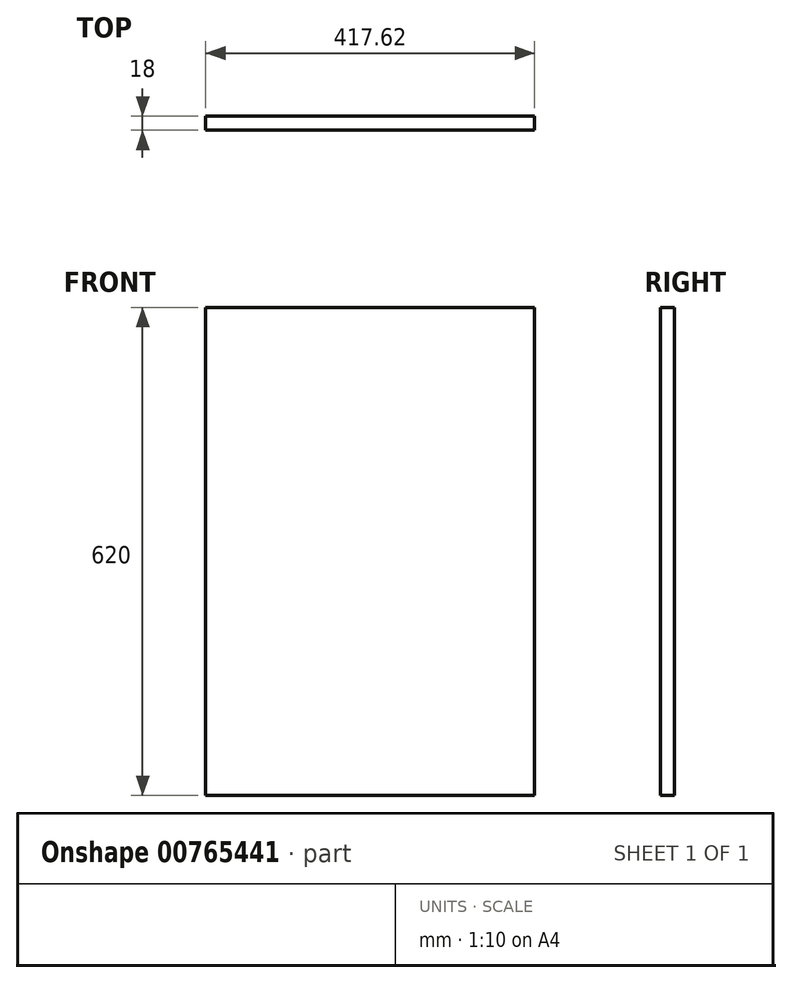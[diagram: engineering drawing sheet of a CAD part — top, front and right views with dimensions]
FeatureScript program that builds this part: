
annotation { "Feature Type Name" : "Feature", "Feature Type Description" : "" }
export const myFeature = defineFeature(function(context is Context, id is Id, definition is map)
    precondition{}
    {
        {
            var Q0;
            Q0=qCreatedBy(makeId("Front.planeOp"),FACE);
            var sketch = newSketch(context, id + "F0", { "sketchPlane" : qUnion([Q0])});
            skLineSegment(sketch, "E0.bottom", {"start": v(-208.81, -310) * mm, "end": v(208.81, -310) * mm});
            skLineSegment(sketch, "E0.top", {"start": v(-208.81, 310) * mm, "end": v(208.81, 310) * mm});
            skLineSegment(sketch, "E0.left", {"start": v(-208.81, -310) * mm, "end": v(-208.81, 310) * mm});
            skLineSegment(sketch, "E0.right", {"start": v(208.81, -310) * mm, "end": v(208.81, 310) * mm});
            skPoint(sketch, "E0.middle", {"position": v(0, 0) * mm});
            skSolve(sketch);
        }
        {
            var Q0;
            Q0 = qSketchRegion(id + "F0", true);
            extrude(context, id + "F1", {"entities" : qUnion([Q0]), "depth" : 18 * mm, "offsetDistance" : 25 * mm});
        }
    });
